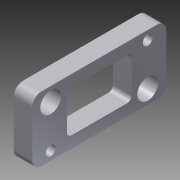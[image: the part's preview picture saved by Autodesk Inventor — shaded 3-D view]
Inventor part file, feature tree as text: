
AUTODESK INVENTOR PART (.ipt)
format: ipt  version: 2013 (Build 170138000, 138)  size: 133,632 bytes
history: native  units: in
note: dims shown in document units (in); Inventor stores cm internally (conversion verified against a paired STEP export)
features: extrude x1, fillet x1, sketch x1
ambient origin geometry x8: Origin, YZ Plane, XZ Plane, XY Plane, X Axis, Y Axis, Z Axis, Center Point
bodies: Solid1 (feature_tree)
feature tree (3):
  extrude  "Extrusion1"  Depth=0.3125in
  fillet  "Fillet1"  Radius=1.75in
  sketch  "Sketch1"  dims[d0=0.625in d2=0.3125in d3=1.75in d4=0.375in d5=0.375in d6=3.625in d7=0.5in d8=0.5in d11=0.5625in d12=0.5625in d13=0.5in d14=0.0in d15=1.125in d16=1.75in d17=0.25in d18=0.125in d19=0.266in d20=0.266in d21=0.325in d22=0.5in d23=0.325in d24=0.5in]
